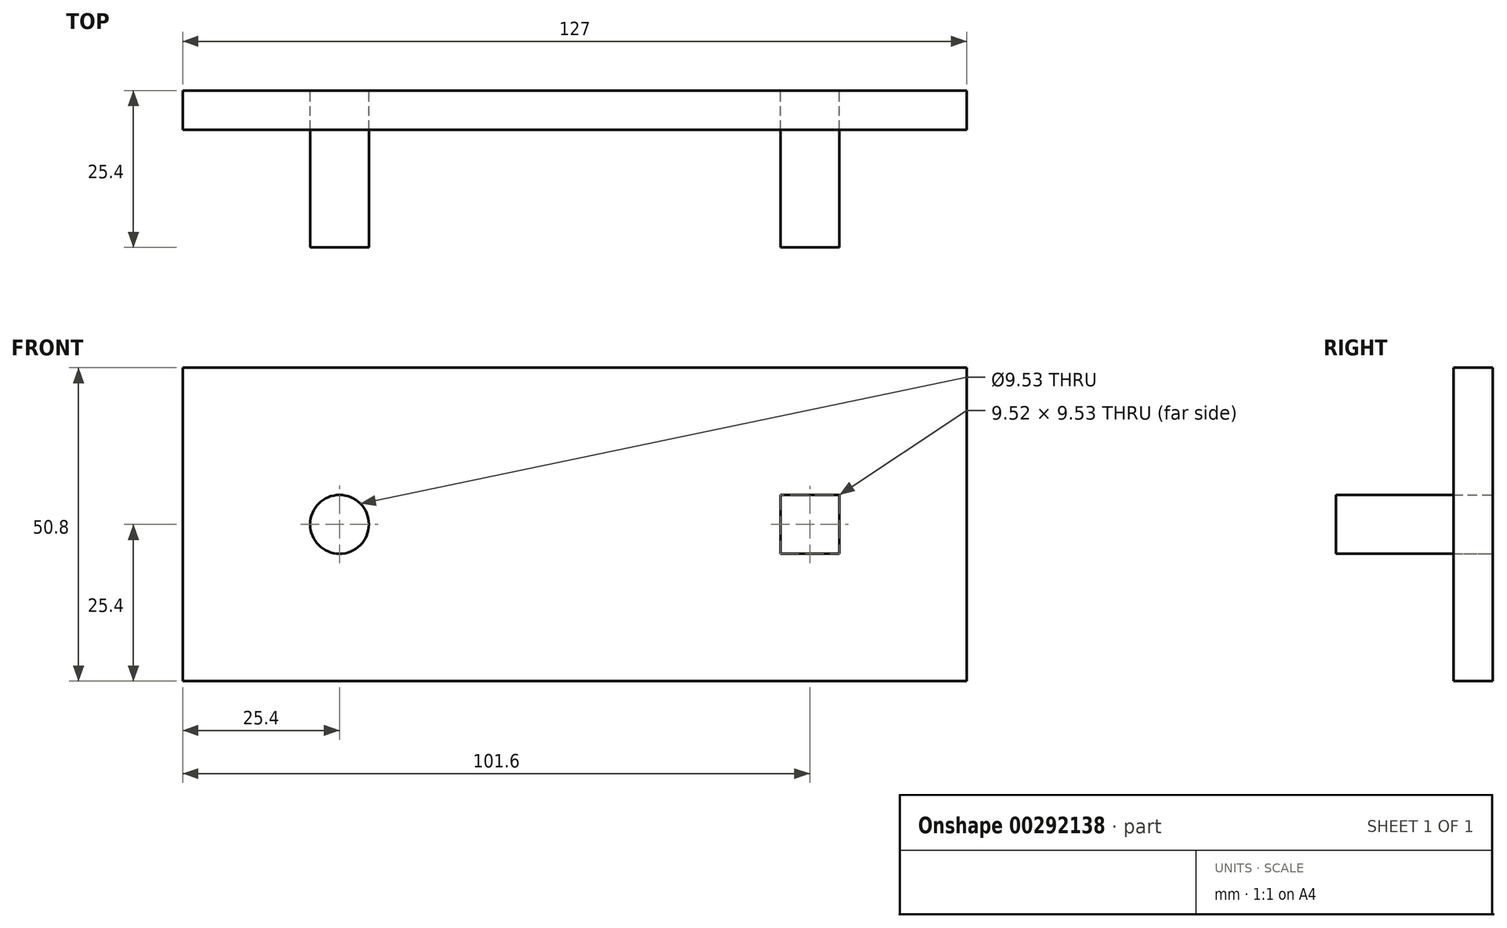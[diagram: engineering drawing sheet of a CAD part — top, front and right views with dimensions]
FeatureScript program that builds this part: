
annotation { "Feature Type Name" : "Feature", "Feature Type Description" : "" }
export const myFeature = defineFeature(function(context is Context, id is Id, definition is map)
    precondition{}
    {
        {
            var Q0;
            Q0=qCreatedBy(makeId("Front.planeOp"),FACE);
            var sketch = newSketch(context, id + "F0", { "sketchPlane" : qUnion([Q0])});
            skLineSegment(sketch, "E0.bottom", {"start": v(63.5, 25.4) * mm, "end": v(-63.5, 25.4) * mm});
            skLineSegment(sketch, "E0.top", {"start": v(63.5, -25.4) * mm, "end": v(-63.5, -25.4) * mm});
            skLineSegment(sketch, "E0.left", {"start": v(63.5, 25.4) * mm, "end": v(63.5, -25.4) * mm});
            skLineSegment(sketch, "E0.right", {"start": v(-63.5, 25.4) * mm, "end": v(-63.5, -25.4) * mm});
            skPoint(sketch, "E0.middle", {"position": v(0, 0) * mm});
            skCircle(sketch, "E1", {"center": v(-38.1, 0) * mm, "radius": 4.76 * mm});
            skLineSegment(sketch, "E2.bottom", {"start": v(42.86, 4.76) * mm, "end": v(33.34, 4.76) * mm});
            skLineSegment(sketch, "E2.top", {"start": v(42.86, -4.76) * mm, "end": v(33.34, -4.76) * mm});
            skLineSegment(sketch, "E2.left", {"start": v(42.86, 4.76) * mm, "end": v(42.86, -4.76) * mm});
            skLineSegment(sketch, "E2.right", {"start": v(33.34, 4.76) * mm, "end": v(33.34, -4.76) * mm});
            skPoint(sketch, "E2.middle", {"position": v(38.1, 0) * mm});
            skSolve(sketch);
        }
        {
            var Q0;
            Q0=makeQuery(id+"F0.imprint","IMPRINT",FACE,{"disambiguationData":[TD([[makeQuery(id+"F0.imprint","IMPRINT",EDGE,{"derivedFrom":sQuery(id+"F0.wireOp",EDGE,"E1")}),1.0]])]});
            var Q1;
            Q1=makeQuery(id+"F0.imprint","IMPRINT",FACE,{"disambiguationData":[TD([[makeQuery(id+"F0.imprint","IMPRINT",EDGE,{"derivedFrom":sQuery(id+"F0.wireOp",EDGE,"E2.bottom")}),1.0]])]});
            extrude(context, id + "F1", {"entities" : qUnion([Q0, Q1]), "depth" : 25.4 * mm});
        }
        {
            var Q0;
            Q0 = qSketchRegion(id + "F0", true);
            extrude(context, id + "F2", {"entities" : qUnion([Q0]), "depth" : 6.35 * mm});
        }
    });
